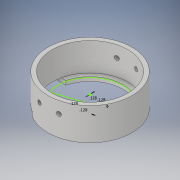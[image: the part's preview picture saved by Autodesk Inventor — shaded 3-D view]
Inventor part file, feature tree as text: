
AUTODESK INVENTOR PART (.ipt)
format: ipt  version: 2018 (Build 220112000, 112)  size: 176,128 bytes
history: native  units: in
note: dims shown in document units (in); Inventor stores cm internally (conversion verified against a paired STEP export)
features: sketch x9, extrude x7
ambient origin geometry x8: Origin, YZ Plane, XZ Plane, XY Plane, X Axis, Y Axis, Z Axis, Center Point
bodies: Solid1 (feature_tree)
feature tree (16):
  extrude  "Extrusion1"  Depth=5.1069in
  extrude  "Extrusion2"  Depth=4.06in
  sketch  "Sketch3"  dims[d5=5.1069in d6=0.25in d7=0.0in]
  extrude  "Extrusion3"  Depth=0.25in TaperAngle=0.0deg
  extrude  "Extrusion8"  Depth=0.3in TaperAngle=0.0deg
  extrude  "Extrusion9"  Depth=6.0in TaperAngle=0.0deg
  extrude  "Extrusion10"  Depth=6.0in TaperAngle=0.0deg
  sketch  "Sketch13"  dims[d36=0.5in]
  extrude  "Extrusion11"  Depth=0.25in TaperAngle=0.0deg
  sketch  "Sketch1"  dims[d0=4.6069in d1=5.1069in]
  sketch  "Sketch2"  dims[d2=1.7125in d3=0.0in d4=4.06in]
  sketch  "Sketch5"  dims[d8=0.128in d9=0.128in d10=0.128in d11=0.128in d12=0.3in d13=0.0in]
  sketch  "Sketch10"  dims[d27=0.2559in d28=6.0in d29=0.0in]
  sketch  "Sketch11"  dims[d30=0.2559in d31=6.0in d32=0.0in]
  sketch  "Sketch12"  dims[d33=0.5in d34=0.25in d35=0.0in]
  sketch  "Sketch14"  dims[d37=0.25in d38=0.0in]
